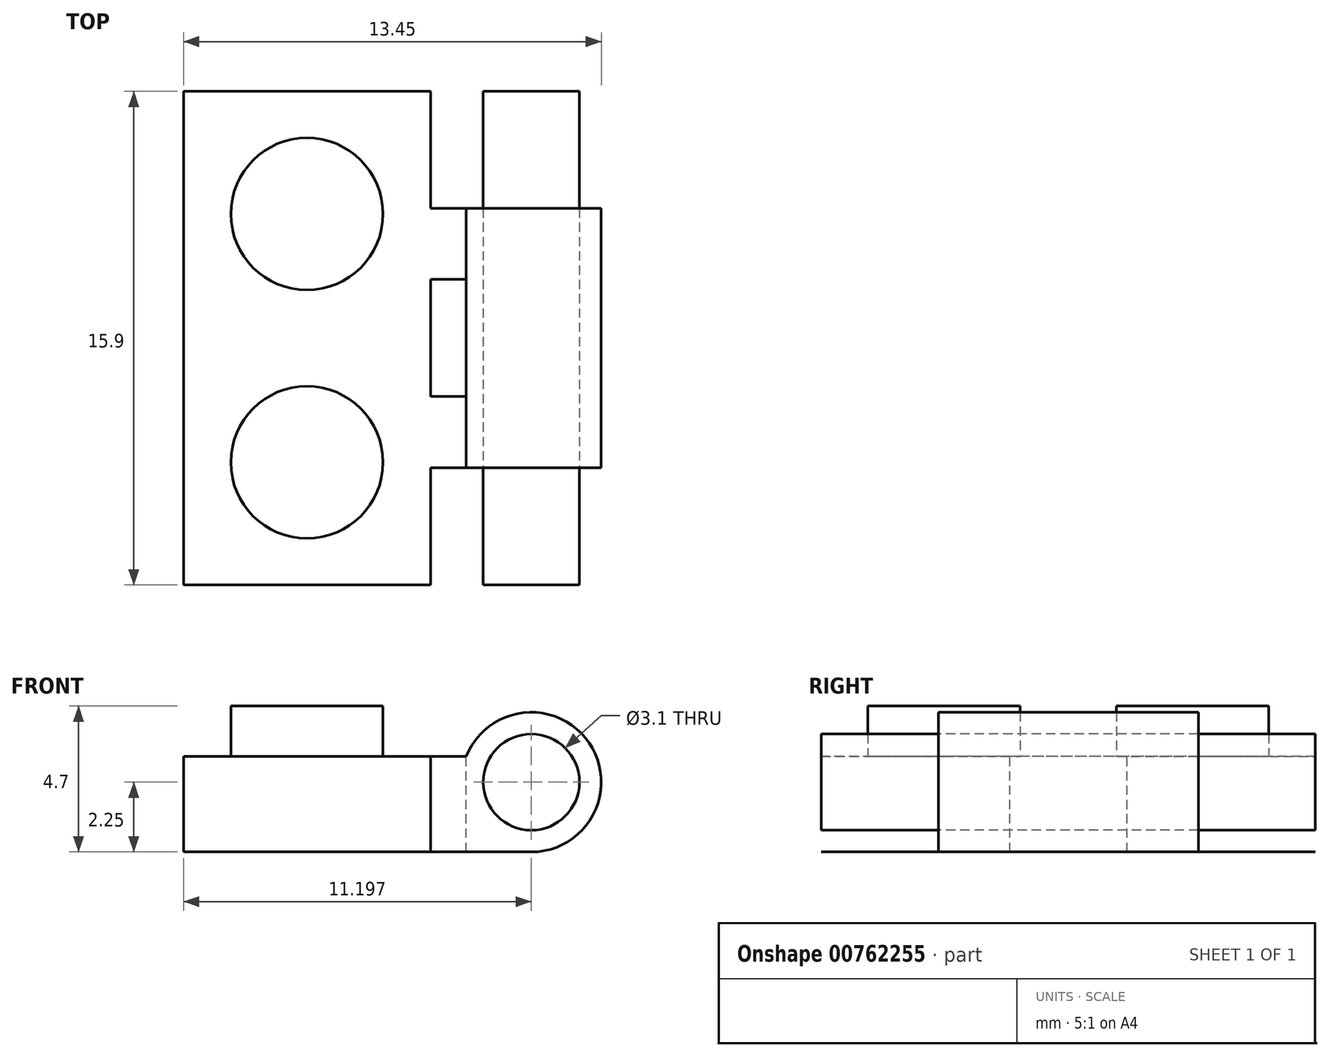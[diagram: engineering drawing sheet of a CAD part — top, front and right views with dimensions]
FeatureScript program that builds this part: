
annotation { "Feature Type Name" : "Feature", "Feature Type Description" : "" }
export const myFeature = defineFeature(function(context is Context, id is Id, definition is map)
    precondition{}
    {
        {
            var Q0;
            Q0=qCreatedBy(makeId("Top.planeOp"),FACE);
            var sketch = newSketch(context, id + "F0", { "sketchPlane" : qUnion([Q0])});
            skLineSegment(sketch, "E0.bottom", {"start": v(0, 0) * mm, "end": v(7.95, 0) * mm});
            skLineSegment(sketch, "E0.top", {"start": v(0, -15.9) * mm, "end": v(7.95, -15.9) * mm});
            skLineSegment(sketch, "E0.left", {"start": v(0, 0) * mm, "end": v(0, -15.9) * mm});
            skLineSegment(sketch, "E0.right", {"start": v(7.95, 0) * mm, "end": v(7.95, -15.9) * mm});
            skCircle(sketch, "E1", {"center": v(3.98, -3.95) * mm, "radius": 2.45 * mm});
            skPoint(sketch, "E1.centerSnap0", {"position": v(3.98, 0) * mm});
            skCircle(sketch, "E2", {"center": v(3.98, -11.95) * mm, "radius": 2.45 * mm});
            skSolve(sketch);
        }
        {
            var Q0;
            Q0 = qSketchRegion(id + "F0", true);
            extrude(context, id + "F1", {"entities" : qUnion([Q0]), "depth" : 3.08 * mm, "offsetDistance" : 25 * mm});
        }
        {
            var Q0;
            Q0=makeQuery(id+"F0.imprint","IMPRINT",FACE,{"disambiguationData":[TD([[makeQuery(id+"F0.imprint","IMPRINT",EDGE,{"derivedFrom":sQuery(id+"F0.wireOp",EDGE,"E2")}),1.0]])]});
            var Q1;
            Q1=makeQuery(id+"F0.imprint","IMPRINT",FACE,{"disambiguationData":[TD([[makeQuery(id+"F0.imprint","IMPRINT",EDGE,{"derivedFrom":sQuery(id+"F0.wireOp",EDGE,"E1")}),1.0]])]});
            extrude(context, id + "F2", {"entities" : qUnion([Q0, Q1]), "operationType" : NewBodyOperationType.ADD, "depth" : 4.7 * mm, "offsetDistance" : 25 * mm});
        }
        {
            var Q0;
            Q0=makeQuery(id+"F1.opExtrude","SWEPT_FACE",FACE,{"disambiguationData":[OSD([sQuery(id+"F0.wireOp",EDGE,"E0.top")])]});
            var sketch = newSketch(context, id + "F3", { "sketchPlane" : qUnion([Q0])});
            skArc(sketch, "E3", {"start": v(11.2, 0) * mm, "mid": v(13.06, 3.51) * mm, "end": v(9.1, 3.08) * mm});
            skLineSegment(sketch, "E4", {"start": v(7.95, 0) * mm, "end": v(11.2, 0) * mm});
            skLineSegment(sketch, "E5", {"start": v(7.95, 3.08) * mm, "end": v(9.1, 3.08) * mm});
            skCircle(sketch, "E6", {"center": v(11.2, 2.25) * mm, "radius": 1.55 * mm});
            skSolve(sketch);
        }
        {
            var Q0;
            Q0=makeQuery(id+"F3.imprint","IMPRINT",FACE,{"disambiguationData":[TD([[makeQuery(id+"F3.imprint","IMPRINT",EDGE,{"derivedFrom":sQuery(id+"F3.wireOp",EDGE,"E3")}),1.0]])]});
            extrude(context, id + "F4", {"entities" : qUnion([Q0]), "operationType" : NewBodyOperationType.ADD, "oppositeDirection" : true, "depth" : 15.9 * mm, "offsetDistance" : 25 * mm});
        }
        {
            var Q0;
            Q0=makeQuery(id+"F4.boolean.opBoolean","MERGE",FACE,{"derivedFrom":[makeQuery(id+"F1.opExtrude","CAP_FACE",FACE,{"disambiguationData":[OSD([sQuery(id+"F0.wireOp",EDGE,"E0.bottom"),sQuery(id+"F0.wireOp",EDGE,"E0.top"),sQuery(id+"F0.wireOp",EDGE,"E0.left"),sQuery(id+"F0.wireOp",EDGE,"E0.right"),sQuery(id+"F0.wireOp",EDGE,"E1"),sQuery(id+"F0.wireOp",EDGE,"E2")])],"isStart":false}),makeQuery(id+"F4.opExtrude","SWEPT_FACE",FACE,{"disambiguationData":[OSD([sQuery(id+"F3.wireOp",EDGE,"E5")])]})]});
            var sketch = newSketch(context, id + "F5", { "sketchPlane" : qUnion([Q0])});
            skPoint(sketch, "E7", {"position": v(7.95, 0) * mm});
            skLineSegment(sketch, "E8", {"start": v(7.95, 0) * mm, "end": v(7.95, -3.77) * mm});
            skLineSegment(sketch, "E9", {"start": v(7.95, -3.77) * mm, "end": v(9.1, -3.77) * mm});
            skLineSegment(sketch, "E10", {"start": v(9.1, -3.77) * mm, "end": v(9.1, 0) * mm});
            skLineSegment(sketch, "E11", {"start": v(9.1, 0) * mm, "end": v(7.95, 0) * mm});
            skLineSegment(sketch, "E12", {"start": v(7.95, -6.06) * mm, "end": v(9.1, -6.06) * mm});
            skLineSegment(sketch, "E13", {"start": v(9.1, -6.06) * mm, "end": v(9.1, -9.83) * mm});
            skLineSegment(sketch, "E14", {"start": v(9.1, -9.83) * mm, "end": v(7.95, -9.83) * mm});
            skLineSegment(sketch, "E15", {"start": v(7.95, -9.83) * mm, "end": v(7.95, -6.06) * mm});
            skLineSegment(sketch, "E16", {"start": v(7.95, -15.9) * mm, "end": v(7.95, -12.13) * mm});
            skLineSegment(sketch, "E17", {"start": v(7.95, -12.13) * mm, "end": v(9.1, -12.13) * mm});
            skLineSegment(sketch, "E18", {"start": v(9.1, -12.13) * mm, "end": v(9.1, -15.9) * mm});
            skLineSegment(sketch, "E19", {"start": v(9.1, -15.9) * mm, "end": v(7.95, -15.9) * mm});
            skLineSegment(sketch, "E20", {"start": v(7.95, -3.77) * mm, "end": v(7.95, -6.06) * mm});
            skLineSegment(sketch, "E21", {"start": v(7.95, -12.13) * mm, "end": v(7.95, -9.83) * mm});
            skLineSegment(sketch, "E22", {"start": v(9.1, 0) * mm, "end": v(10.36, 0) * mm});
            skLineSegment(sketch, "E23", {"start": v(10.36, 0) * mm, "end": v(10.36, -3.77) * mm});
            skLineSegment(sketch, "E24", {"start": v(10.36, -3.77) * mm, "end": v(9.1, -3.77) * mm});
            skLineSegment(sketch, "E25", {"start": v(9.1, -6.06) * mm, "end": v(10.36, -6.06) * mm});
            skLineSegment(sketch, "E26", {"start": v(10.36, -6.06) * mm, "end": v(10.36, -9.83) * mm});
            skLineSegment(sketch, "E27", {"start": v(10.36, -9.83) * mm, "end": v(9.1, -9.83) * mm});
            skLineSegment(sketch, "E28", {"start": v(9.1, -12.13) * mm, "end": v(10.36, -12.13) * mm});
            skLineSegment(sketch, "E29", {"start": v(10.36, -12.13) * mm, "end": v(10.36, -15.9) * mm});
            skLineSegment(sketch, "E30", {"start": v(10.36, -15.9) * mm, "end": v(9.1, -15.9) * mm});
            skSolve(sketch);
        }
        {
            var Q0;
            Q0=makeQuery(id+"F5.imprint","IMPRINT",FACE,{"disambiguationData":[TD([[makeQuery(id+"F5.imprint","IMPRINT",EDGE,{"derivedFrom":sQuery(id+"F5.wireOp",EDGE,"E16")}),-1.0]])]});
            var Q1;
            Q1=makeQuery(id+"F5.imprint","IMPRINT",FACE,{"disambiguationData":[TD([[makeQuery(id+"F5.imprint","IMPRINT",EDGE,{"derivedFrom":sQuery(id+"F5.wireOp",EDGE,"E12")}),-1.0]])]});
            var Q2;
            Q2=makeQuery(id+"F5.imprint","IMPRINT",FACE,{"disambiguationData":[TD([[makeQuery(id+"F5.imprint","IMPRINT",EDGE,{"derivedFrom":sQuery(id+"F5.wireOp",EDGE,"E8")}),1.0]])]});
            extrude(context, id + "F6", {"entities" : qUnion([Q0, Q1, Q2]), "operationType" : NewBodyOperationType.REMOVE, "oppositeDirection" : true, "depth" : 25 * mm, "offsetDistance" : 25 * mm});
        }
        {
            var Q0;
            Q0 = qSketchRegion(id + "F3", true);
            extrude(context, id + "F7", {"entities" : qUnion([Q0]), "oppositeDirection" : true, "depth" : 15.9 * mm, "offsetDistance" : 25 * mm});
        }
        {
            var Q0;
            {var subQ0=sQuery(id+"F3.wireOp",EDGE,"E3");var subQ3=sQuery(id+"F0.wireOp",EDGE,"E0.right");var subQ4=sQuery(id+"F0.wireOp",EDGE,"E0.top");var subQ5=sQuery(id+"F3.wireOp",EDGE,"E4");var subQ6=sQuery(id+"F3.wireOp",EDGE,"E6");Q0=makeQuery(id+"F6.boolean.opBoolean","SPLIT",FACE,{"disambiguationData":[TD([makeQuery(id+"F4.opExtrude","SWEPT_FACE",FACE,{"disambiguationData":[OSD([subQ0])]})])],"derivedFrom":makeQuery(id+"F4.boolean.opBoolean","MERGE",FACE,{"derivedFrom":[makeQuery(id+"F1.opExtrude","SWEPT_FACE",FACE,{"disambiguationData":[OSD([subQ4])]}),makeQuery(id+"F4.opExtrude","CAP_FACE",FACE,{"disambiguationData":[OSD([subQ4,subQ3,subQ0,subQ5,sQuery(id+"F3.wireOp",EDGE,"E5"),subQ6])],"isStart":true})]})});}
            var sketch = newSketch(context, id + "F8", { "sketchPlane" : qUnion([Q0])});
            skArc(sketch, "E31", {"start": v(11.2, 0) * mm, "mid": v(13.06, 3.51) * mm, "end": v(9.1, 3.08) * mm});
            skCircle(sketch, "E32", {"center": v(11.2, 2.25) * mm, "radius": 1.55 * mm});
            skLineSegment(sketch, "E33", {"start": v(9.1, 3.08) * mm, "end": v(7.95, 3.08) * mm});
            skLineSegment(sketch, "E34", {"start": v(7.95, 3.08) * mm, "end": v(7.95, 0) * mm});
            skLineSegment(sketch, "E35", {"start": v(7.95, 0) * mm, "end": v(11.2, 0) * mm});
            skSolve(sketch);
        }
        {
            var Q0;
            {var subQ0=sQuery(id+"F8.wireOp",EDGE,"E31");Q0=makeQuery(id+"F8.imprint","IMPRINT",FACE,{"disambiguationData":[TD([[makeQuery(id+"F8.imprint","IMPRINT",EDGE,{"derivedFrom":subQ0}),1.0]])]});}
            var Q1;
            Q1=makeQuery(id+"F8.imprint","IMPRINT",FACE,{"disambiguationData":[TD([[makeQuery(id+"F8.imprint","IMPRINT",EDGE,{"derivedFrom":sQuery(id+"F8.wireOp",EDGE,"E33")}),1.0]])]});
            extrude(context, id + "F9", {"entities" : qUnion([Q0, Q1]), "operationType" : NewBodyOperationType.REMOVE, "oppositeDirection" : true, "depth" : 3.77 * mm, "offsetDistance" : 25 * mm});
        }
        {
            var Q0;
            {var subQ0=sQuery(id+"F3.wireOp",EDGE,"E3");var subQ3=sQuery(id+"F0.wireOp",EDGE,"E0.right");var subQ4=sQuery(id+"F0.wireOp",EDGE,"E0.top");var subQ5=sQuery(id+"F0.wireOp",EDGE,"E0.bottom");var subQ6=sQuery(id+"F3.wireOp",EDGE,"E4");var subQ7=sQuery(id+"F3.wireOp",EDGE,"E6");Q0=makeQuery(id+"F6.boolean.opBoolean","SPLIT",FACE,{"disambiguationData":[TD([makeQuery(id+"F4.opExtrude","SWEPT_FACE",FACE,{"disambiguationData":[OSD([subQ0])]})])],"derivedFrom":makeQuery(id+"F4.boolean.opBoolean","MERGE",FACE,{"derivedFrom":[makeQuery(id+"F1.opExtrude","SWEPT_FACE",FACE,{"disambiguationData":[OSD([subQ5])]}),makeQuery(id+"F4.opExtrude","CAP_FACE",FACE,{"disambiguationData":[OSD([subQ4,subQ3,subQ0,subQ6,sQuery(id+"F3.wireOp",EDGE,"E5"),subQ7])],"isStart":false})]})});}
            var sketch = newSketch(context, id + "F10", { "sketchPlane" : qUnion([Q0])});
            skCircle(sketch, "E36", {"center": v(-11.2, 2.25) * mm, "radius": 1.55 * mm});
            skArc(sketch, "E37", {"start": v(-9.1, 3.08) * mm, "mid": v(-13.06, 3.51) * mm, "end": v(-11.2, 0) * mm});
            skLineSegment(sketch, "E38", {"start": v(-9.1, 3.08) * mm, "end": v(-7.96, 3.08) * mm});
            skLineSegment(sketch, "E39", {"start": v(-7.96, 3.08) * mm, "end": v(-7.96, 0) * mm});
            skLineSegment(sketch, "E40", {"start": v(-7.96, 0) * mm, "end": v(-11.2, 0) * mm});
            skSolve(sketch);
        }
        {
            var Q0;
            Q0 = qSketchRegion(id + "F10", true);
            extrude(context, id + "F11", {"entities" : qUnion([Q0]), "operationType" : NewBodyOperationType.REMOVE, "oppositeDirection" : true, "depth" : 3.77 * mm, "offsetDistance" : 25 * mm});
        }
    });
